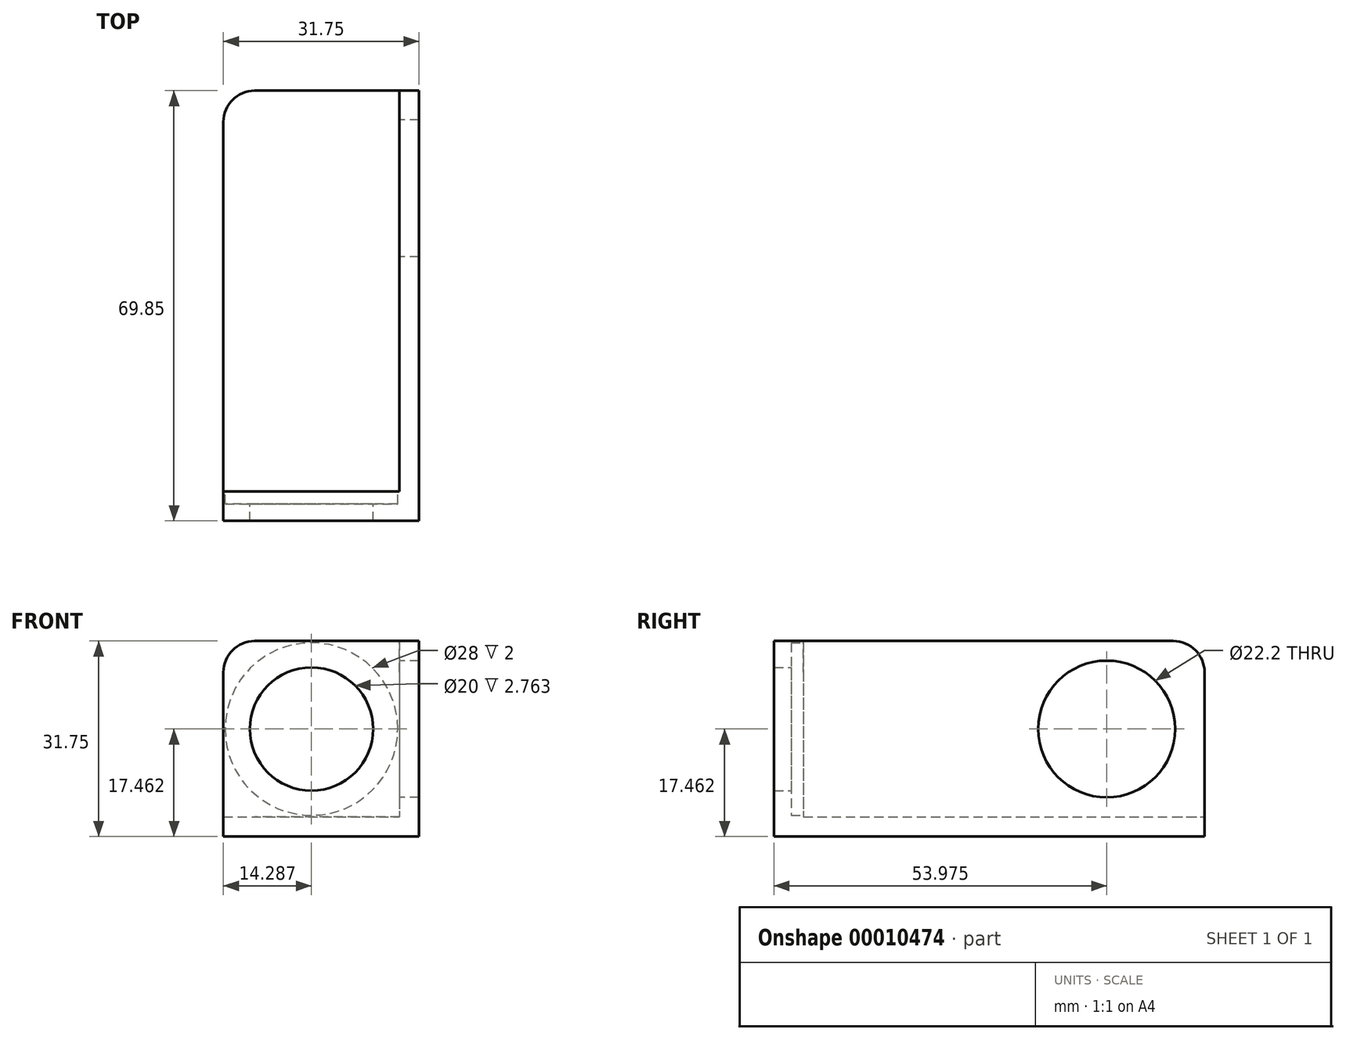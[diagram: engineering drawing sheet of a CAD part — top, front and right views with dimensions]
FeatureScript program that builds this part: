
annotation { "Feature Type Name" : "Feature", "Feature Type Description" : "" }
export const myFeature = defineFeature(function(context is Context, id is Id, definition is map)
    precondition{}
    {
        {
            var Q0;
            Q0=qCreatedBy(makeId("Front.planeOp"),FACE);
            var sketch = newSketch(context, id + "F0", { "sketchPlane" : qUnion([Q0])});
            skLineSegment(sketch, "E0", {"start": v(0, 0) * mm, "end": v(31.75, 0) * mm});
            skLineSegment(sketch, "E1", {"start": v(31.75, 0) * mm, "end": v(31.75, 31.75) * mm});
            skLineSegment(sketch, "E2", {"start": v(31.75, 31.75) * mm, "end": v(28.57, 31.75) * mm});
            skLineSegment(sketch, "E3", {"start": v(28.57, 31.75) * mm, "end": v(28.58, 3.18) * mm});
            skLineSegment(sketch, "E4", {"start": v(28.58, 3.18) * mm, "end": v(0, 3.18) * mm});
            skLineSegment(sketch, "E5", {"start": v(0, 3.18) * mm, "end": v(0, 0) * mm});
            skSolve(sketch);
        }
        {
            var Q0;
            Q0 = qSketchRegion(id + "F0", true);
            extrude(context, id + "F1", {"entities" : qUnion([Q0]), "depth" : 69.85 * mm});
        }
        {
            var Q0;
            Q0=makeQuery(id+"F1.opExtrude","SWEPT_FACE",FACE,{"disambiguationData":[OSD([sQuery(id+"F0.wireOp",EDGE,"E4")])]});
            var sketch = newSketch(context, id + "F2", { "sketchPlane" : qUnion([Q0])});
            skLineSegment(sketch, "E6.bottom", {"start": v(0, -69.85) * mm, "end": v(28.58, -69.85) * mm});
            skLineSegment(sketch, "E6.top", {"start": v(0, -65.09) * mm, "end": v(28.58, -65.09) * mm});
            skLineSegment(sketch, "E6.left", {"start": v(0, -69.85) * mm, "end": v(0, -65.09) * mm});
            skLineSegment(sketch, "E6.right", {"start": v(28.58, -69.85) * mm, "end": v(28.58, -65.09) * mm});
            skSolve(sketch);
        }
        {
            var Q0;
            Q0 = qSketchRegion(id + "F2", true);
            var Q1;
            Q1=makeQuery(id+"F1.opExtrude","SWEPT_FACE",FACE,{"disambiguationData":[OSD([sQuery(id+"F0.wireOp",EDGE,"E2")])]});
            extrude(context, id + "F3", {"entities" : qUnion([Q0]), "operationType" : NewBodyOperationType.ADD, "endBound" : BoundingType.UP_TO_SURFACE, "endBoundEntityFace" : qUnion([Q1]), "depth" : 25 * mm});
        }
        {
            var Q0;
            Q0=makeQuery(id+"F3.opExtrude","SWEPT_FACE",FACE,{"disambiguationData":[OSD([sQuery(id+"F2.wireOp",EDGE,"E6.top")])]});
            var sketch = newSketch(context, id + "F4", { "sketchPlane" : qUnion([Q0])});
            skLineSegment(sketch, "E7", {"start": v(-28.58, 17.46) * mm, "end": v(0, 17.46) * mm, "construction": true});
            skCircle(sketch, "E8", {"center": v(-14.29, 17.46) * mm, "radius": 14 * mm});
            skSolve(sketch);
        }
        {
            var Q0;
            Q0 = qSketchRegion(id + "F4", true);
            extrude(context, id + "F5", {"entities" : qUnion([Q0]), "operationType" : NewBodyOperationType.REMOVE, "oppositeDirection" : true, "depth" : 2 * mm});
        }
        {
            var Q0;
            Q0=makeQuery(id+"F5.boolean.opBoolean","COPY",FACE,{"derivedFrom":makeQuery(id+"F5.opExtrude","CAP_FACE",FACE,{"disambiguationData":[OSD([sQuery(id+"F4.wireOp",EDGE,"E8")])],"isStart":false})});
            var sketch = newSketch(context, id + "F6", { "sketchPlane" : qUnion([Q0])});
            skCircle(sketch, "E9", {"center": v(-14.29, 17.46) * mm, "radius": 10 * mm});
            skSolve(sketch);
        }
        {
            var Q0;
            Q0 = qSketchRegion(id + "F6", true);
            extrude(context, id + "F7", {"entities" : qUnion([Q0]), "operationType" : NewBodyOperationType.REMOVE, "endBound" : BoundingType.UP_TO_NEXT, "oppositeDirection" : true, "depth" : 25 * mm});
        }
        {
            var Q0;
            Q0=makeQuery(id+"F1.opExtrude","SWEPT_FACE",FACE,{"disambiguationData":[OSD([sQuery(id+"F0.wireOp",EDGE,"E3")])]});
            var sketch = newSketch(context, id + "F8", { "sketchPlane" : qUnion([Q0])});
            skPoint(sketch, "E10", {"position": v(15.88, 17.46) * mm});
            skCircle(sketch, "E11", {"center": v(15.88, 17.46) * mm, "radius": 11.1 * mm});
            skLineSegment(sketch, "E12", {"start": v(65.09, 17.46) * mm, "end": v(0, 17.46) * mm});
            skSolve(sketch);
        }
        {
            var Q0;
            Q0 = qSketchRegion(id + "F8", true);
            extrude(context, id + "F9", {"entities" : qUnion([Q0]), "operationType" : NewBodyOperationType.REMOVE, "endBound" : BoundingType.UP_TO_NEXT, "oppositeDirection" : true, "depth" : 25 * mm});
        }
        {
            var Q0;
            Q0=makeQuery(id+"F1.opExtrude","CAP_EDGE",EDGE,{"disambiguationData":[OSD([sQuery(id+"F0.wireOp",EDGE,"E5")])],"isStart":true});
            var Q1;
            Q1=makeQuery(id+"F3.opExtrude","CAP_EDGE",EDGE,{"disambiguationData":[OSD([sQuery(id+"F2.wireOp",EDGE,"E6.left")])],"isStart":false});
            var Q2;
            Q2=makeQuery(id+"F1.opExtrude","CAP_EDGE",EDGE,{"disambiguationData":[OSD([sQuery(id+"F0.wireOp",EDGE,"E2")])],"isStart":true});
            fillet(context, id + "F10", {"entities" : qUnion([Q0, Q1, Q2]), "radius" : 5.08 * mm, "tangentPropagation" : true, "allowEdgeOverflow" : false});
        }
    });
